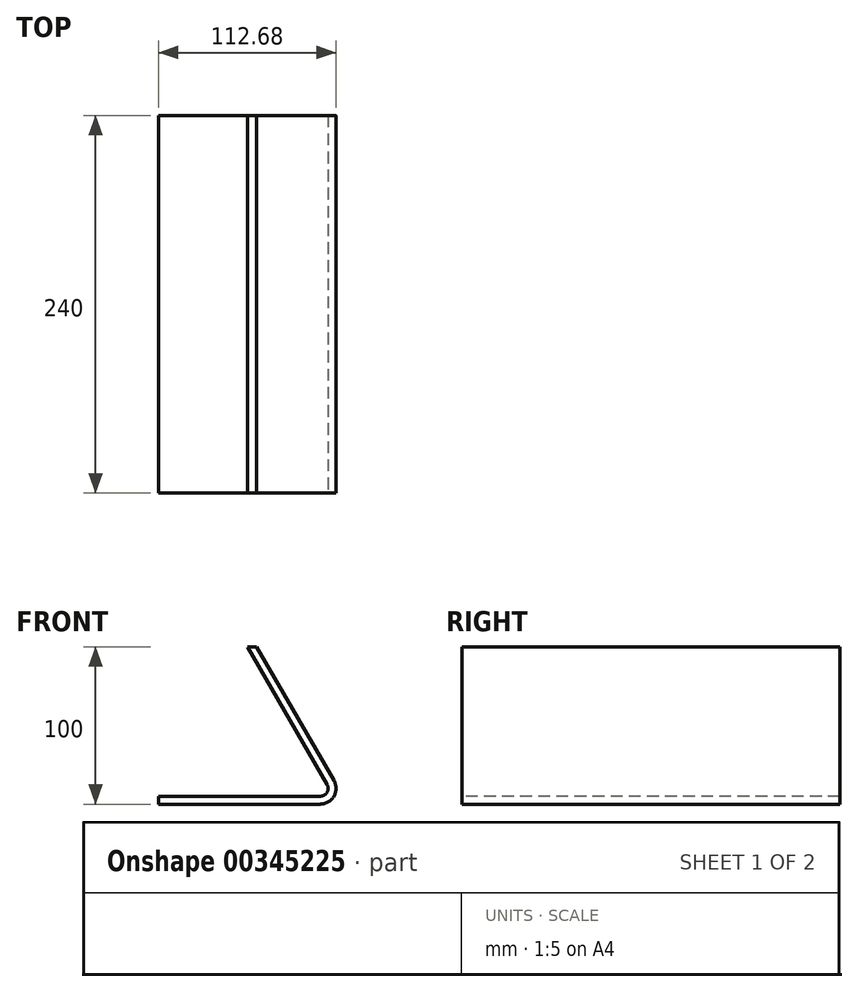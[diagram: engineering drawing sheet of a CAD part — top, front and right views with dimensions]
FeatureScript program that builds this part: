
annotation { "Feature Type Name" : "Feature", "Feature Type Description" : "" }
export const myFeature = defineFeature(function(context is Context, id is Id, definition is map)
    precondition{}
    {
        {
            var Q0;
            Q0=qCreatedBy(makeId("Front.planeOp"),FACE);
            var sketch = newSketch(context, id + "F0", { "sketchPlane" : qUnion([Q0])});
            skLineSegment(sketch, "E0.top", {"start": v(-60, -50) * mm, "end": v(42.68, -50) * mm});
            skLineSegment(sketch, "E0.left", {"start": v(-60, 50) * mm, "end": v(-60, -50) * mm});
            skPoint(sketch, "E0.middle", {"position": v(0, 0) * mm});
            skLineSegment(sketch, "E1", {"start": v(51.34, -35) * mm, "end": v(2.26, 50) * mm});
            skLineSegment(sketch, "E2", {"start": v(-60, 50) * mm, "end": v(2.26, 50) * mm});
            skPoint(sketch, "E3.visualSharp", {"position": v(60, -50) * mm});
            skArc(sketch, "E3.filletArc", {"start": v(42.68, -50) * mm, "mid": v(51.34, -45) * mm, "end": v(51.34, -35) * mm});
            skSolve(sketch);
        }
        {
            var Q0;
            Q0=qSketchRegion(id+"F0",true);
            extrude(context, id + "F1", {"entities" : qUnion([Q0]), "depth" : 240 * mm});
        }
        {
            var Q0;
            Q0=makeQuery(id+"F1.opExtrude","CAP_FACE",FACE,{"disambiguationData":[OSD([sQuery(id+"F0.wireOp",EDGE,"E0.top"),sQuery(id+"F0.wireOp",EDGE,"E0.left"),sQuery(id+"F0.wireOp",EDGE,"E1"),sQuery(id+"F0.wireOp",EDGE,"E2"),sQuery(id+"F0.wireOp",EDGE,"E3.filletArc")])],"isStart":false});
            var sketch = newSketch(context, id + "F2", { "sketchPlane" : qUnion([Q0])});
            skPoint(sketch, "E4.visualSharp", {"position": v(100, -50) * mm});
            skPoint(sketch, "E5.visualSharp", {"position": v(42.68, -40) * mm});
            skPoint(sketch, "E6.visualSharp", {"position": v(60, -50) * mm});
            skLineSegment(sketch, "E7.0", {"start": v(47, -37.5) * mm, "end": v(-3.5, 50) * mm});
            skArc(sketch, "E7.1", {"start": v(42.68, -45) * mm, "mid": v(47, -42.5) * mm, "end": v(47, -37.5) * mm});
            skLineSegment(sketch, "E8", {"start": v(-60, 50) * mm, "end": v(-60, -45) * mm});
            skLineSegment(sketch, "E9", {"start": v(-3.5, 50) * mm, "end": v(-60, 50) * mm});
            skLineSegment(sketch, "E10", {"start": v(42.68, -45) * mm, "end": v(-60, -45) * mm});
            skSolve(sketch);
        }
        {
            var Q0;
            Q0=qSketchRegion(id+"F2",true);
            extrude(context, id + "F3", {"entities" : qUnion([Q0]), "operationType" : NewBodyOperationType.REMOVE, "oppositeDirection" : true, "depth" : 240 * mm});
        }
    });
